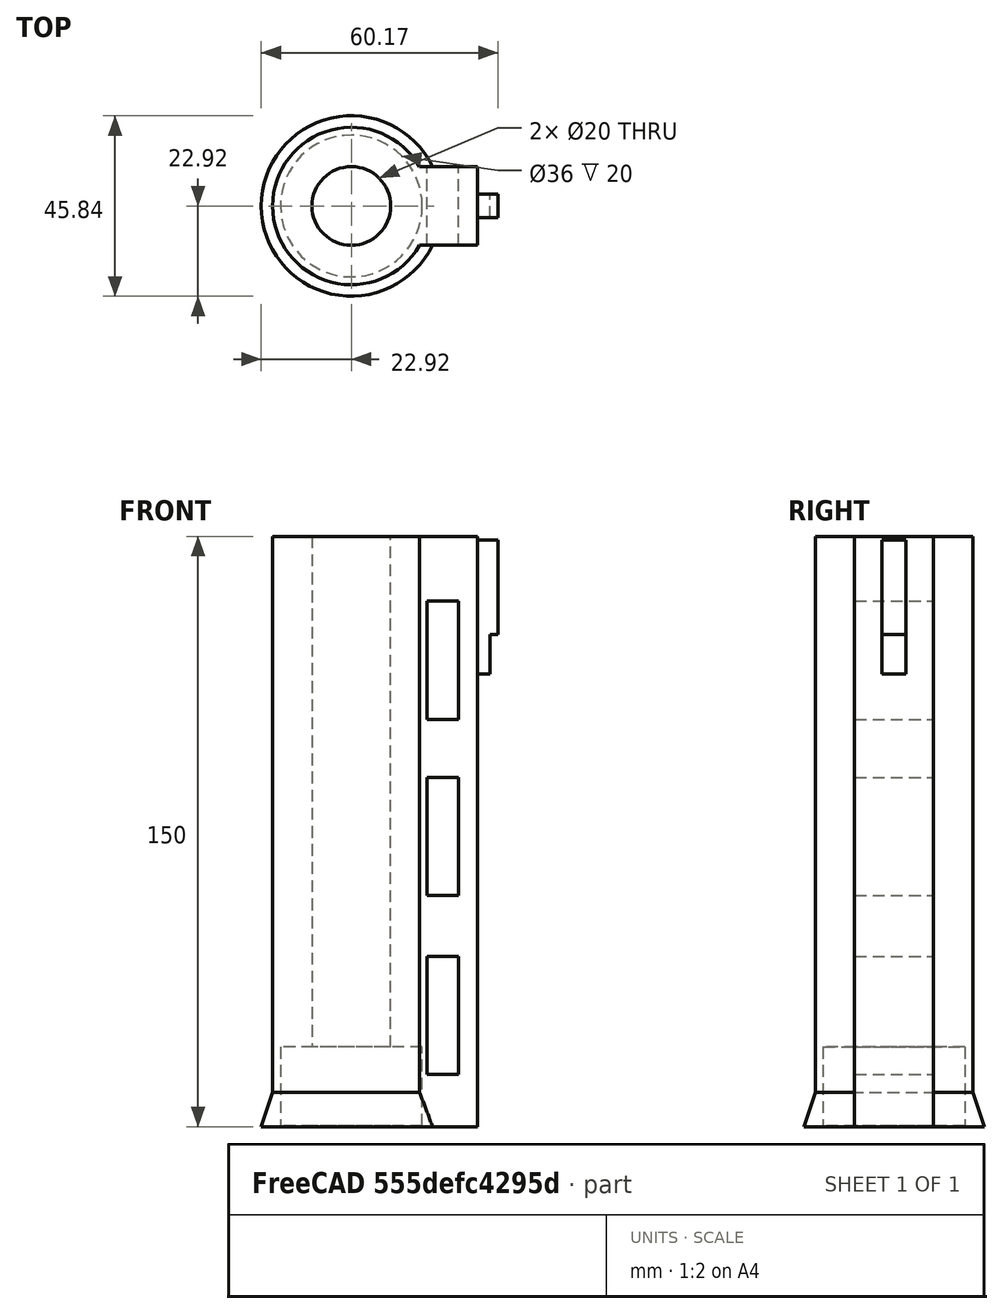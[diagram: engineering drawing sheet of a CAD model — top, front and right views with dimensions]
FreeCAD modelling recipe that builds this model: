
FCSTD DOCUMENT  (FreeCAD 0.20R29410 (Git))
Label: lachesisbarrel0
License: All rights reserved
LicenseURL: http://en.wikipedia.org/wiki/All_rights_reserved
objects: Part::Box×11, Part::MultiFuse×10, Part::Cut×6, Part::Cylinder×5, Part::Cone×1, Part::Feature×1
note: 34 computed .brp shape members not serialized (recipe doc carries the construction recipe); baked Part::Feature solids carry a one-line shape summary decoded from their .brp

FEATURE [Part::Cylinder] Cylinder
  Angle = 360
  AttacherType = Attacher::AttachEngine3D
  FirstAngle = 0
  Height = 290
  Radius = 20
  SecondAngle = 0
FEATURE [Part::Box] Box  label="Cube"
  AttacherType = Attacher::AttachEngine3D
  Height = 290
  Length = 8
  Placement = pos=(17.25,-10,0) rot=(0,0,1;0rad)
  Width = 20
FEATURE [Part::Cylinder] Cylinder001
  Angle = 360
  AttacherType = Attacher::AttachEngine3D
  FirstAngle = 0
  Height = 140
  Radius = 25
  SecondAngle = 0
FEATURE [Part::Cone] Cone
  Angle = 360
  AttacherType = Attacher::AttachEngine3D
  Height = 15
  Placement = pos=(0,0,139.75) rot=(0,0,1;0rad)
  Radius1 = 23
  Radius2 = 18
FEATURE [Part::Box] Box001  label="Cube001"
  AttacherType = Attacher::AttachEngine3D
  Height = 290
  Length = 8
  Placement = pos=(24,-10,0) rot=(0,0,1;0rad)
  Width = 20
FEATURE [Part::Box] Box002  label="Cube002"
  AttacherType = Attacher::AttachEngine3D
  Height = 24
  Length = 10
  Placement = pos=(27.25,-10,0) rot=(0,0,1;0rad)
  Width = 6
FEATURE [Part::MultiFuse] Fusion  label="MainBarrel"
  Shapes = -> [Cylinder,Box]
FEATURE [Part::MultiFuse] Fusion001  label="RearBarrel"
  Shapes = -> [Cone,Cylinder001]
FEATURE [Part::Box] Box003  label="Cube003"
  AttacherType = Attacher::AttachEngine3D
  Height = 24
  Length = 10
  Placement = pos=(27.25,4,0) rot=(0,0,1;0rad)
  Width = 6
FEATURE [Part::Box] Box004  label="Cube004"
  AttacherType = Attacher::AttachEngine3D
  Height = 24
  Length = 10
  Placement = pos=(27.25,-3,10) rot=(0,0,1;0rad)
  Width = 6
FEATURE [Part::Box] Box005  label="Cube005"
  AttacherType = Attacher::AttachEngine3D
  Height = 34
  Length = 8
  Placement = pos=(27.25,-3,0) rot=(0,0,1;0rad)
  Width = 6
FEATURE [Part::MultiFuse] Fusion002  label="frontSight"
  Placement = pos=(0,0,255) rot=(0,0,1;0rad)
  Shapes = -> [Box004,Box005]
FEATURE [Part::MultiFuse] Fusion003
  Shapes = -> [Box003,Box001]
FEATURE [Part::MultiFuse] Fusion004  label="rearSight"
  Shapes = -> [Fusion003,Box002]
FEATURE [Part::MultiFuse] Fusion005  label="IronSights"
  Shapes = -> [Fusion004,Fusion002]
FEATURE [Part::MultiFuse] Fusion006  label="BarrelAssembly"
  Shapes = -> [Fusion001,Fusion]
FEATURE [Part::MultiFuse] Fusion007  label="MainBarrelAssembly"
  Shapes = -> [Fusion005,Fusion006]
FEATURE [Part::Box] Box006  label="Cube006"
  AttacherType = Attacher::AttachEngine3D
  Height = 30
  Length = 8
  Placement = pos=(19.25,-22.75,153.25) rot=(0,0,1;0rad)
  Width = 50
FEATURE [Part::Box] Box007  label="Cube007"
  AttacherType = Attacher::AttachEngine3D
  Height = 30
  Length = 8
  Placement = pos=(19.25,-22.75,198.75) rot=(0,0,1;0rad)
  Width = 50
FEATURE [Part::Box] Box008  label="Cube008"
  AttacherType = Attacher::AttachEngine3D
  Height = 30
  Length = 8
  Placement = pos=(19.25,-22.75,243.5) rot=(0,0,1;0rad)
  Width = 50
FEATURE [Part::Cut] Cut
  Base = -> Fusion007
  Tool = -> Box006
FEATURE [Part::Cut] Cut001
  Base = -> Cut
  Tool = -> Box007
FEATURE [Part::Cut] Cut002
  Base = -> Cut001
  Tool = -> Box008
FEATURE [Part::Cylinder] Cylinder002
  Angle = 360
  AttacherType = Attacher::AttachEngine3D
  FirstAngle = 0
  Height = 20
  Placement = pos=(0,0,7.25) rot=(0,0,1;0rad)
  Radius = 10
  SecondAngle = 0
FEATURE [Part::Cylinder] Cylinder003
  Angle = 360
  AttacherType = Attacher::AttachEngine3D
  FirstAngle = 0
  Height = 290
  Placement = pos=(0,0,5.25) rot=(0,0,1;0rad)
  Radius = 10
  SecondAngle = 0
FEATURE [Part::MultiFuse] Fusion008
  Shapes = -> [Cylinder002,Cut002]
FEATURE [Part::Cut] Cut003
  Base = -> Fusion008
  Tool = -> Cylinder003
FEATURE [Part::Box] Box009  label="Cube009"
  AttacherType = Attacher::AttachEngine3D
  Height = 10
  Length = 10
  Width = 10
FEATURE [Part::MultiFuse] Fusion009
  Shapes = -> [Box009,Cut003]
FEATURE [Part::Box] Box010  label="Cube010"
  AttacherType = Attacher::AttachEngine3D
  Height = 140
  Length = 110
  Placement = pos=(-47.25,-41.25,0) rot=(0,0,1;0rad)
  Width = 101
FEATURE [Part::Cut] Cut004
  Base = -> Fusion009
  Tool = -> Box010
FEATURE [Part::Cylinder] Cylinder004
  Angle = 360
  AttacherType = Attacher::AttachEngine3D
  FirstAngle = 0
  Height = 20
  Placement = pos=(0,0,140.25) rot=(0,0,1;0rad)
  Radius = 18
  SecondAngle = 0
FEATURE [Part::Cut] Cut005
  Base = -> Cut004
  Tool = -> Cylinder004
FEATURE [Part::Feature] Cut005_solid  label="Cut005 (Solid)"
  shape: bbox 60.17 x 45.83 x 150 mm, 50 faces (baked)
